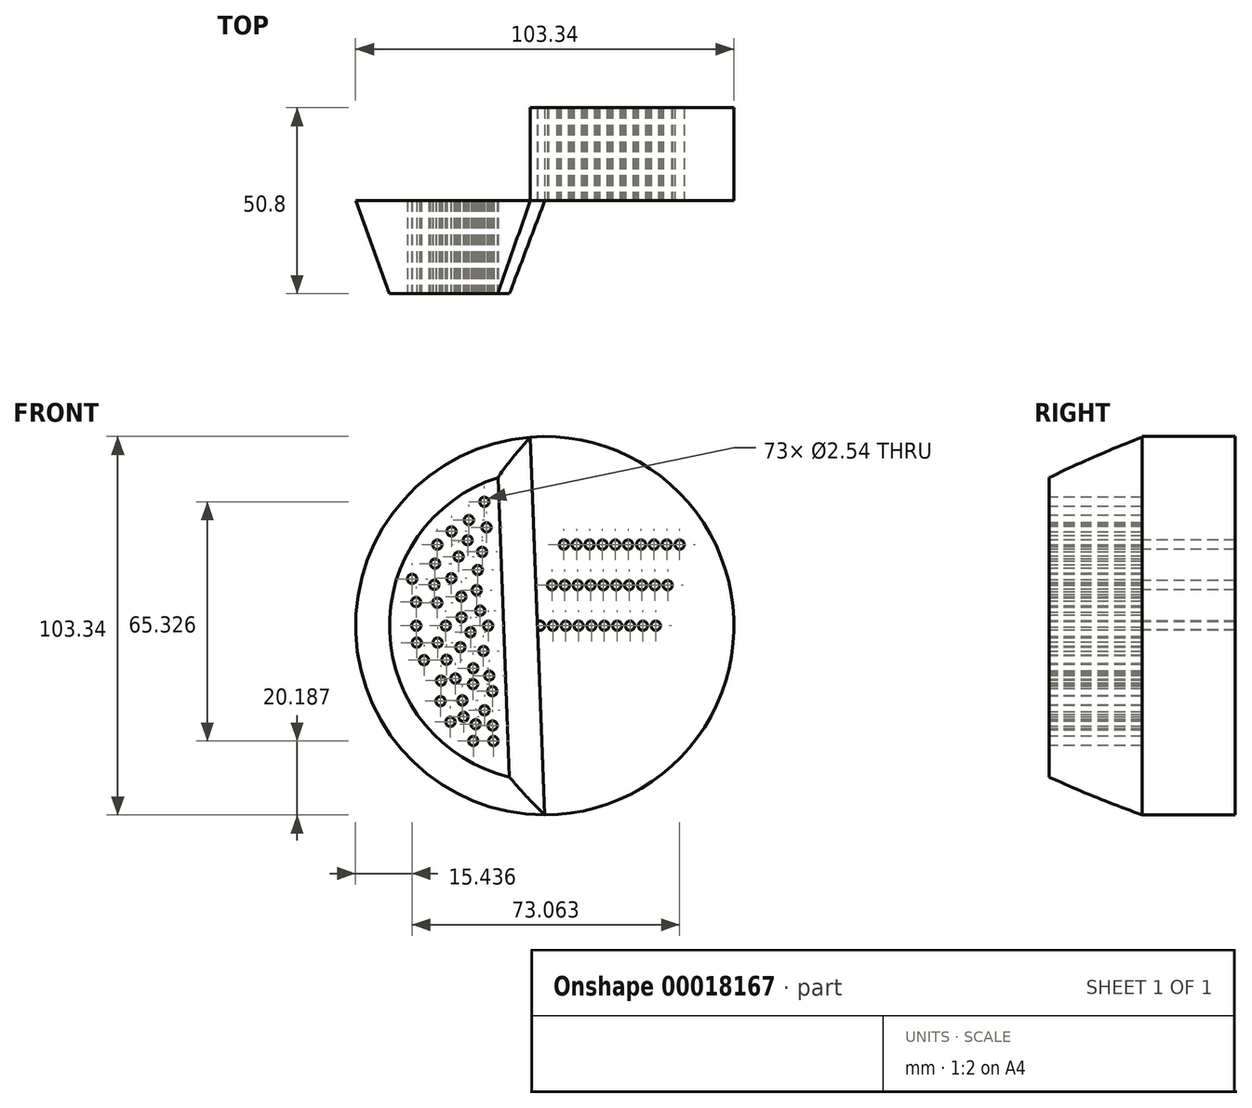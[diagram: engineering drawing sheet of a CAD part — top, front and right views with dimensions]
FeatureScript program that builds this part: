
annotation { "Feature Type Name" : "Feature", "Feature Type Description" : "" }
export const myFeature = defineFeature(function(context is Context, id is Id, definition is map)
    precondition{}
    {
        {
            var Q0;
            Q0=qCreatedBy(makeId("Front.planeOp"),FACE);
            var sketch = newSketch(context, id + "F0", { "sketchPlane" : qUnion([Q0])});
            skCircle(sketch, "E0", {"center": v(0, 0) * mm, "radius": 51.67 * mm});
            skLineSegment(sketch, "E1", {"start": v(-3.98, 51.51) * mm, "end": v(0, -51.67) * mm});
            skSolve(sketch);
        }
        {
            var Q0;
            {var subQ0=sQuery(id+"F0.wireOp",EDGE,"E1");Q0=makeQuery(id+"F0.imprint","IMPRINT",FACE,{"disambiguationData":[TD([[makeQuery(id+"F0.imprint","IMPRINT",EDGE,{"derivedFrom":subQ0}),-1.0]])]});}
            extrude(context, id + "F1", {"entities" : qUnion([Q0]), "depth" : 25.4 * mm, "hasDraft" : true, "draftAngle" : 20 * degree, "draftPullDirection" : true});
        }
        {
            var Q0;
            {var subQ0=sQuery(id+"F0.wireOp",EDGE,"E1");Q0=makeQuery(id+"F0.imprint","IMPRINT",FACE,{"disambiguationData":[TD([[makeQuery(id+"F0.imprint","IMPRINT",EDGE,{"derivedFrom":subQ0}),1.0]])]});}
            extrude(context, id + "F2", {"entities" : qUnion([Q0]), "oppositeDirection" : true, "depth" : 25.4 * mm});
        }
        {
            var Q0;
            Q0=makeQuery(id+"F1.opExtrude","CAP_FACE",FACE,{"disambiguationData":[OSD([sQuery(id+"F0.wireOp",EDGE,"E0"),sQuery(id+"F0.wireOp",EDGE,"E1")])],"isStart":false});
            var sketch = newSketch(context, id + "F3", { "sketchPlane" : qUnion([Q0])});
            skPoint(sketch, "E2", {"position": v(-16.5, 33.84) * mm});
            skPoint(sketch, "E3", {"position": v(-15.9, 26.86) * mm});
            skPoint(sketch, "E4", {"position": v(-20.74, 28.84) * mm});
            skPoint(sketch, "E5", {"position": v(-25.47, 25.77) * mm});
            skPoint(sketch, "E6", {"position": v(-21.05, 23.31) * mm});
            skPoint(sketch, "E7", {"position": v(-17.12, 20.19) * mm});
            skPoint(sketch, "E8", {"position": v(-18.3, 15.23) * mm});
            skPoint(sketch, "E9", {"position": v(-23.52, 18.9) * mm});
            skPoint(sketch, "E10", {"position": v(-29.35, 22.14) * mm});
            skPoint(sketch, "E11", {"position": v(-29.96, 16.96) * mm});
            skPoint(sketch, "E12", {"position": v(-25.52, 12.97) * mm});
            skPoint(sketch, "E13", {"position": v(-18.6, 9.71) * mm});
            skPoint(sketch, "E14", {"position": v(-22.8, 7.95) * mm});
            skPoint(sketch, "E15", {"position": v(-30.16, 11.18) * mm});
            skPoint(sketch, "E16", {"position": v(-29.35, 6.28) * mm});
            skPoint(sketch, "E17", {"position": v(-36.23, 12.79) * mm});
            skPoint(sketch, "E18", {"position": v(-35.14, 6.47) * mm});
            skPoint(sketch, "E19", {"position": v(-35.1, 0) * mm});
            skPoint(sketch, "E20", {"position": v(-27.03, 0) * mm});
            skPoint(sketch, "E21", {"position": v(-22.75, 2.28) * mm});
            skPoint(sketch, "E22", {"position": v(-17.65, 4.1) * mm});
            skPoint(sketch, "E23", {"position": v(-15.45, 0) * mm});
            skPoint(sketch, "E24", {"position": v(-20.28, -1.77) * mm});
            skPoint(sketch, "E25", {"position": v(-16.75, -6.9) * mm});
            skPoint(sketch, "E26", {"position": v(-23.05, -5.85) * mm});
            skPoint(sketch, "E27", {"position": v(-29.27, -4.61) * mm});
            skPoint(sketch, "E28", {"position": v(-34.96, -4.61) * mm});
            skPoint(sketch, "E29", {"position": v(-32.97, -9.4) * mm});
            skPoint(sketch, "E30", {"position": v(-26.85, -9.3) * mm});
            skPoint(sketch, "E31", {"position": v(-19.56, -11.63) * mm});
            skPoint(sketch, "E32", {"position": v(-15.17, -13.64) * mm});
            skPoint(sketch, "E33", {"position": v(-14.31, -17.9) * mm});
            skPoint(sketch, "E34", {"position": v(-19.6, -15.96) * mm});
            skPoint(sketch, "E35", {"position": v(-24.4, -14.43) * mm});
            skPoint(sketch, "E36", {"position": v(-28.32, -15) * mm});
            skPoint(sketch, "E37", {"position": v(-28.45, -20.6) * mm});
            skPoint(sketch, "E38", {"position": v(-22.51, -20.41) * mm});
            skPoint(sketch, "E39", {"position": v(-16.45, -23.1) * mm});
            skPoint(sketch, "E40", {"position": v(-14.25, -27.26) * mm});
            skPoint(sketch, "E41", {"position": v(-14.03, -31.48) * mm});
            skPoint(sketch, "E42", {"position": v(-19.52, -31.48) * mm});
            skPoint(sketch, "E43", {"position": v(-18.88, -26.9) * mm});
            skPoint(sketch, "E44", {"position": v(-22.18, -24.9) * mm});
            skPoint(sketch, "E45", {"position": v(-25.78, -26.25) * mm});
            skSolve(sketch);
        }
        {
            var Q0;
            Q0=makeQuery(id+"F2.opExtrude","CAP_FACE",FACE,{"disambiguationData":[OSD([sQuery(id+"F0.wireOp",EDGE,"E0"),sQuery(id+"F0.wireOp",EDGE,"E1")])],"isStart":true});
            var sketch = newSketch(context, id + "F4", { "sketchPlane" : qUnion([Q0])});
            skPoint(sketch, "E46", {"position": v(30.32, 0) * mm});
            skPoint(sketch, "E47.0.1.0", {"position": v(26.8, 0) * mm});
            skPoint(sketch, "E47.0.2.0", {"position": v(23.3, 0) * mm});
            skPoint(sketch, "E47.0.3.0", {"position": v(19.78, 0) * mm});
            skPoint(sketch, "E47.0.4.0", {"position": v(16.27, 0) * mm});
            skPoint(sketch, "E47.0.5.0", {"position": v(12.76, 0) * mm});
            skPoint(sketch, "E47.0.6.0", {"position": v(9.24, 0) * mm});
            skPoint(sketch, "E47.0.7.0", {"position": v(5.73, 0) * mm});
            skPoint(sketch, "E47.0.8.0", {"position": v(2.22, 0) * mm});
            skPoint(sketch, "E47.0.9.0", {"position": v(-1.3, 0) * mm});
            skPoint(sketch, "E47.1.0.0", {"position": v(33.57, 11.08) * mm});
            skPoint(sketch, "E47.1.1.0", {"position": v(30.06, 11.08) * mm});
            skPoint(sketch, "E47.1.2.0", {"position": v(26.55, 11.08) * mm});
            skPoint(sketch, "E47.1.3.0", {"position": v(23.04, 11.08) * mm});
            skPoint(sketch, "E47.1.4.0", {"position": v(19.52, 11.08) * mm});
            skPoint(sketch, "E47.1.5.0", {"position": v(16, 11.08) * mm});
            skPoint(sketch, "E47.1.6.0", {"position": v(12.5, 11.08) * mm});
            skPoint(sketch, "E47.1.7.0", {"position": v(8.98, 11.08) * mm});
            skPoint(sketch, "E47.1.8.0", {"position": v(5.47, 11.08) * mm});
            skPoint(sketch, "E47.1.9.0", {"position": v(1.96, 11.08) * mm});
            skPoint(sketch, "E47.2.0.0", {"position": v(36.83, 22.16) * mm});
            skPoint(sketch, "E47.2.1.0", {"position": v(33.32, 22.16) * mm});
            skPoint(sketch, "E47.2.2.0", {"position": v(29.8, 22.16) * mm});
            skPoint(sketch, "E47.2.3.0", {"position": v(26.29, 22.16) * mm});
            skPoint(sketch, "E47.2.4.0", {"position": v(22.78, 22.16) * mm});
            skPoint(sketch, "E47.2.5.0", {"position": v(19.26, 22.16) * mm});
            skPoint(sketch, "E47.2.6.0", {"position": v(15.75, 22.16) * mm});
            skPoint(sketch, "E47.2.7.0", {"position": v(12.24, 22.16) * mm});
            skPoint(sketch, "E47.2.8.0", {"position": v(8.72, 22.16) * mm});
            skPoint(sketch, "E47.2.9.0", {"position": v(5.21, 22.16) * mm});
            skSolve(sketch);
        }
        {
            var Q0;
            Q0=sQuery(id+"F4.wireOp",VERTEX,"E46");
            var Q1;
            Q1=makeQuery(id+"F2.opExtrude","SWEPT_BODY",BODY,{"disambiguationData":[OSD([sQuery(id+"F0.wireOp",EDGE,"E0"),sQuery(id+"F0.wireOp",EDGE,"E1")])]});
            hole(context, id + "F5", {"style" : HoleStyle.SIMPLE, "holeDiameter" : 2.54 * mm, "endStyle" : HoleEndStyle.THROUGH, "locations" : qUnion([Q0]), "scope" : qUnion([Q1])});
        }
        {
            var Q0;
            Q0=sQuery(id+"F3.wireOp",VERTEX,"E2");
            var Q1;
            Q1=sQuery(id+"F3.wireOp",VERTEX,"E3");
            var Q2;
            Q2=sQuery(id+"F3.wireOp",VERTEX,"E4");
            var Q3;
            Q3=sQuery(id+"F3.wireOp",VERTEX,"E5");
            var Q4;
            Q4=sQuery(id+"F3.wireOp",VERTEX,"E6");
            var Q5;
            Q5=sQuery(id+"F3.wireOp",VERTEX,"E7");
            var Q6;
            Q6=sQuery(id+"F3.wireOp",VERTEX,"E9");
            var Q7;
            Q7=sQuery(id+"F3.wireOp",VERTEX,"E16");
            var Q8;
            Q8=sQuery(id+"F3.wireOp",VERTEX,"E27");
            var Q9;
            Q9=sQuery(id+"F3.wireOp",VERTEX,"E15");
            var Q10;
            Q10=sQuery(id+"F3.wireOp",VERTEX,"E28");
            var Q11;
            Q11=sQuery(id+"F3.wireOp",VERTEX,"E17");
            var Q12;
            Q12=sQuery(id+"F3.wireOp",VERTEX,"E21");
            var Q13;
            Q13=sQuery(id+"F3.wireOp",VERTEX,"E20");
            var Q14;
            Q14=sQuery(id+"F3.wireOp",VERTEX,"E18");
            var Q15;
            Q15=sQuery(id+"F3.wireOp",VERTEX,"E19");
            var Q16;
            Q16=sQuery(id+"F3.wireOp",VERTEX,"E12");
            var Q17;
            Q17=sQuery(id+"F3.wireOp",VERTEX,"E11");
            var Q18;
            Q18=sQuery(id+"F3.wireOp",VERTEX,"E10");
            var Q19;
            Q19=sQuery(id+"F3.wireOp",VERTEX,"E22");
            var Q20;
            Q20=sQuery(id+"F3.wireOp",VERTEX,"E42");
            var Q21;
            Q21=sQuery(id+"F3.wireOp",VERTEX,"E39");
            var Q22;
            Q22=sQuery(id+"F3.wireOp",VERTEX,"E43");
            var Q23;
            Q23=sQuery(id+"F3.wireOp",VERTEX,"E26");
            var Q24;
            Q24=sQuery(id+"F3.wireOp",VERTEX,"E23");
            var Q25;
            Q25=sQuery(id+"F3.wireOp",VERTEX,"E24");
            var Q26;
            Q26=sQuery(id+"F3.wireOp",VERTEX,"E33");
            var Q27;
            Q27=sQuery(id+"F3.wireOp",VERTEX,"E32");
            var Q28;
            Q28=sQuery(id+"F3.wireOp",VERTEX,"E44");
            var Q29;
            Q29=sQuery(id+"F3.wireOp",VERTEX,"E40");
            var Q30;
            Q30=sQuery(id+"F3.wireOp",VERTEX,"E29");
            var Q31;
            Q31=sQuery(id+"F3.wireOp",VERTEX,"E30");
            var Q32;
            Q32=sQuery(id+"F3.wireOp",VERTEX,"E45");
            var Q33;
            Q33=sQuery(id+"F3.wireOp",VERTEX,"E31");
            var Q34;
            Q34=sQuery(id+"F3.wireOp",VERTEX,"E34");
            var Q35;
            Q35=sQuery(id+"F3.wireOp",VERTEX,"E38");
            var Q36;
            Q36=sQuery(id+"F3.wireOp",VERTEX,"E35");
            var Q37;
            Q37=sQuery(id+"F3.wireOp",VERTEX,"E37");
            var Q38;
            Q38=sQuery(id+"F3.wireOp",VERTEX,"E14");
            var Q39;
            Q39=sQuery(id+"F3.wireOp",VERTEX,"E36");
            var Q40;
            Q40=sQuery(id+"F3.wireOp",VERTEX,"E13");
            var Q41;
            Q41=sQuery(id+"F3.wireOp",VERTEX,"E25");
            var Q42;
            Q42=sQuery(id+"F3.wireOp",VERTEX,"E8");
            var Q43;
            Q43=sQuery(id+"F3.wireOp",VERTEX,"E41");
            var Q44;
            Q44=makeQuery(id+"F1.opExtrude","SWEPT_BODY",BODY,{"disambiguationData":[OSD([sQuery(id+"F0.wireOp",EDGE,"E0"),sQuery(id+"F0.wireOp",EDGE,"E1")])]});
            hole(context, id + "F6", {"style" : HoleStyle.SIMPLE, "holeDiameter" : 2.54 * mm, "endStyle" : HoleEndStyle.THROUGH, "locations" : qUnion([Q0, Q1, Q2, Q3, Q4, Q5, Q6, Q7, Q8, Q9, Q10, Q11, Q12, Q13, Q14, Q15, Q16, Q17, Q18, Q19, Q20, Q21, Q22, Q23, Q24, Q25, Q26, Q27, Q28, Q29, Q30, Q31, Q32, Q33, Q34, Q35, Q36, Q37, Q38, Q39, Q40, Q41, Q42, Q43]), "scope" : qUnion([Q44])});
        }
        {
            var Q0;
            Q0=sQuery(id+"F4.wireOp",VERTEX,"E47.2.0.0");
            var Q1;
            Q1=sQuery(id+"F4.wireOp",VERTEX,"E47.1.0.0");
            var Q2;
            Q2=sQuery(id+"F4.wireOp",VERTEX,"E47.2.1.0");
            var Q3;
            Q3=sQuery(id+"F4.wireOp",VERTEX,"E47.1.1.0");
            var Q4;
            Q4=sQuery(id+"F4.wireOp",VERTEX,"E47.0.1.0");
            var Q5;
            Q5=sQuery(id+"F4.wireOp",VERTEX,"E47.0.7.0");
            var Q6;
            Q6=sQuery(id+"F4.wireOp",VERTEX,"E47.2.8.0");
            var Q7;
            Q7=sQuery(id+"F4.wireOp",VERTEX,"E47.0.5.0");
            var Q8;
            Q8=sQuery(id+"F4.wireOp",VERTEX,"E47.2.6.0");
            var Q9;
            Q9=sQuery(id+"F4.wireOp",VERTEX,"E47.1.6.0");
            var Q10;
            Q10=sQuery(id+"F4.wireOp",VERTEX,"E47.1.7.0");
            var Q11;
            Q11=sQuery(id+"F4.wireOp",VERTEX,"E47.2.7.0");
            var Q12;
            Q12=sQuery(id+"F3.wireOp",VERTEX,"E32");
            var Q13;
            Q13=sQuery(id+"F4.wireOp",VERTEX,"E47.0.6.0");
            var Q14;
            Q14=sQuery(id+"F4.wireOp",VERTEX,"E47.1.5.0");
            var Q15;
            Q15=sQuery(id+"F4.wireOp",VERTEX,"E47.1.8.0");
            var Q16;
            Q16=sQuery(id+"F4.wireOp",VERTEX,"E47.1.3.0");
            var Q17;
            Q17=sQuery(id+"F4.wireOp",VERTEX,"E47.2.10.0");
            var Q18;
            Q18=sQuery(id+"F4.wireOp",VERTEX,"E47.2.9.0");
            var Q19;
            Q19=sQuery(id+"F4.wireOp",VERTEX,"E47.1.10.0");
            var Q20;
            Q20=sQuery(id+"F4.wireOp",VERTEX,"E47.0.9.0");
            var Q21;
            Q21=sQuery(id+"F4.wireOp",VERTEX,"E47.1.9.0");
            var Q22;
            Q22=sQuery(id+"F4.wireOp",VERTEX,"E47.2.5.0");
            var Q23;
            Q23=sQuery(id+"F3.wireOp",VERTEX,"E22");
            var Q24;
            Q24=sQuery(id+"F3.wireOp",VERTEX,"E14");
            var Q25;
            Q25=sQuery(id+"F4.wireOp",VERTEX,"E47.2.2.0");
            var Q26;
            Q26=sQuery(id+"F4.wireOp",VERTEX,"E47.1.2.0");
            var Q27;
            Q27=sQuery(id+"F3.wireOp",VERTEX,"E23");
            var Q28;
            Q28=sQuery(id+"F3.wireOp",VERTEX,"E13");
            var Q29;
            Q29=sQuery(id+"F4.wireOp",VERTEX,"E47.2.4.0");
            var Q30;
            Q30=sQuery(id+"F4.wireOp",VERTEX,"E47.0.3.0");
            var Q31;
            Q31=sQuery(id+"F4.wireOp",VERTEX,"E47.0.4.0");
            var Q32;
            Q32=sQuery(id+"F4.wireOp",VERTEX,"E47.0.2.0");
            var Q33;
            Q33=sQuery(id+"F4.wireOp",VERTEX,"E47.2.3.0");
            var Q34;
            Q34=sQuery(id+"F4.wireOp",VERTEX,"E47.1.4.0");
            var Q35;
            Q35=sQuery(id+"F4.wireOp",VERTEX,"E47.direction2.end");
            var Q36;
            Q36=sQuery(id+"F4.wireOp",VERTEX,"E47.0.10.0");
            var Q37;
            Q37=sQuery(id+"F4.wireOp",VERTEX,"E47.1.11.0");
            var Q38;
            Q38=sQuery(id+"F4.wireOp",VERTEX,"E47.0.11.0");
            var Q39;
            Q39=sQuery(id+"F4.wireOp",VERTEX,"E47.2.11.0");
            var Q40;
            Q40=sQuery(id+"F4.wireOp",VERTEX,"E47.0.8.0");
            var Q41;
            Q41=makeQuery(id+"F2.opExtrude","SWEPT_BODY",BODY,{"disambiguationData":[OSD([sQuery(id+"F0.wireOp",EDGE,"E0"),sQuery(id+"F0.wireOp",EDGE,"E1")])]});
            hole(context, id + "F7", {"style" : HoleStyle.SIMPLE, "holeDiameter" : 2.54 * mm, "endStyle" : HoleEndStyle.THROUGH, "locations" : qUnion([Q0, Q1, Q2, Q3, Q4, Q5, Q6, Q7, Q8, Q9, Q10, Q11, Q12, Q13, Q14, Q15, Q16, Q17, Q18, Q19, Q20, Q21, Q22, Q23, Q24, Q25, Q26, Q27, Q28, Q29, Q30, Q31, Q32, Q33, Q34, Q35, Q36, Q37, Q38, Q39, Q40]), "scope" : qUnion([Q41])});
        }
    });
